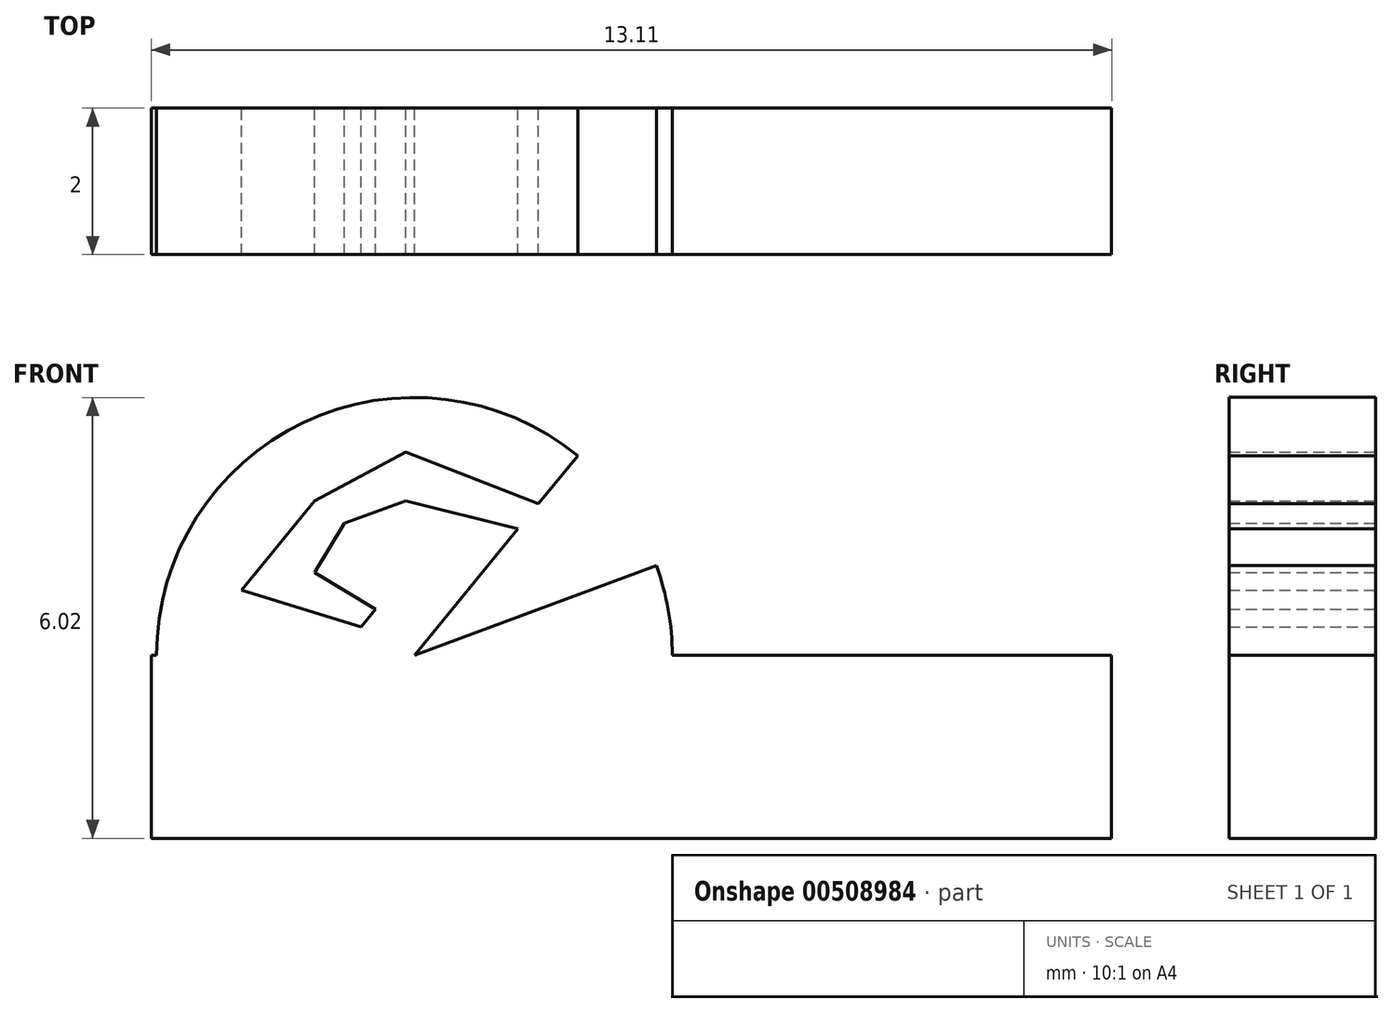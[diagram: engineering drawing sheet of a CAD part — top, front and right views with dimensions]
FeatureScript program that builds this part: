
annotation { "Feature Type Name" : "Feature", "Feature Type Description" : "" }
export const myFeature = defineFeature(function(context is Context, id is Id, definition is map)
    precondition{}
    {
        {
            var Q0;
            Q0=qCreatedBy(makeId("Front.planeOp"),FACE);
            var sketch = newSketch(context, id + "F0", { "sketchPlane" : qUnion([Q0])});
            skLineSegment(sketch, "E0.bottom", {"start": v(-10, 2.5) * mm, "end": v(10, 2.5) * mm});
            skLineSegment(sketch, "E0.top", {"start": v(-10, -2.5) * mm, "end": v(10, -2.5) * mm});
            skLineSegment(sketch, "E0.left", {"start": v(-10, 2.5) * mm, "end": v(-10, -2.5) * mm});
            skLineSegment(sketch, "E0.right", {"start": v(10, 2.5) * mm, "end": v(10, -2.5) * mm});
            skPoint(sketch, "E0.middle", {"position": v(0, 0) * mm});
            skArc(sketch, "E1", {"start": v(-2.89, 2.5) * mm, "mid": v(-2.94, 3.12) * mm, "end": v(-3.1, 3.72) * mm});
            skLineSegment(sketch, "E2", {"start": v(-4.18, 5.22) * mm, "end": v(-4.72, 4.57) * mm});
            skLineSegment(sketch, "E3", {"start": v(-6.41, 2.5) * mm, "end": v(-3.1, 3.72) * mm});
            skArc(sketch, "E4.trimOffspring", {"start": v(-4.18, 5.22) * mm, "mid": v(-7.92, 5.68) * mm, "end": v(-9.93, 2.5) * mm});
            skPoint(sketch, "E5.orphan", {"position": v(0, 4.87) * mm});
            skLineSegment(sketch, "E6", {"start": v(-4.72, 4.57) * mm, "end": v(-6.53, 5.28) * mm});
            skLineSegment(sketch, "E7", {"start": v(-6.53, 5.28) * mm, "end": v(-7.77, 4.6) * mm});
            skLineSegment(sketch, "E8", {"start": v(-7.77, 4.6) * mm, "end": v(-8.77, 3.39) * mm});
            skLineSegment(sketch, "E9", {"start": v(-8.77, 3.39) * mm, "end": v(-7.14, 2.89) * mm});
            skLineSegment(sketch, "E10", {"start": v(-7.14, 2.89) * mm, "end": v(-6.94, 3.13) * mm});
            skLineSegment(sketch, "E11", {"start": v(-6.94, 3.13) * mm, "end": v(-7.77, 3.63) * mm});
            skLineSegment(sketch, "E12", {"start": v(-7.77, 3.63) * mm, "end": v(-7.36, 4.3) * mm});
            skLineSegment(sketch, "E13", {"start": v(-7.36, 4.3) * mm, "end": v(-6.53, 4.6) * mm});
            skLineSegment(sketch, "E14", {"start": v(-6.53, 4.6) * mm, "end": v(-5, 4.23) * mm});
            skLineSegment(sketch, "E15.trimOffspring", {"start": v(-5, 4.23) * mm, "end": v(-6.41, 2.5) * mm});
            skSolve(sketch);
        }
        {
            var Q0;
            Q0=makeQuery(id+"F0.imprint","IMPRINT",FACE,{"disambiguationData":[TD([[makeQuery(id+"F0.imprint","IMPRINT",EDGE,{"derivedFrom":sQuery(id+"F0.wireOp",EDGE,"E0.top")}),1.0]])]});
            var Q1;
            Q1=makeQuery(id+"F0.imprint","IMPRINT",FACE,{"disambiguationData":[TD([[makeQuery(id+"F0.imprint","IMPRINT",EDGE,{"derivedFrom":sQuery(id+"F0.wireOp",EDGE,"E2")}),-1.0]])]});
            var Q2;
            {var subQ0=sQuery(id+"F0.wireOp",EDGE,"E1");Q2=makeQuery(id+"F0.imprint","IMPRINT",FACE,{"disambiguationData":[TD([[makeQuery(id+"F0.imprint","IMPRINT",EDGE,{"derivedFrom":subQ0}),1.0]])]});}
            extrude(context, id + "F1", {"entities" : qUnion([Q0, Q1, Q2]), "depth" : 2 * mm});
        }
        {
            var Q0;
            Q0=makeQuery(id+"F1.opExtrude","CAP_FACE",FACE,{"disambiguationData":[OSD([sQuery(id+"F0.wireOp",EDGE,"E0.bottom"),sQuery(id+"F0.wireOp",EDGE,"E0.top"),sQuery(id+"F0.wireOp",EDGE,"E0.left"),sQuery(id+"F0.wireOp",EDGE,"E0.right"),sQuery(id+"F0.wireOp",EDGE,"E1"),sQuery(id+"F0.wireOp",EDGE,"E2"),sQuery(id+"F0.wireOp",EDGE,"E3"),sQuery(id+"F0.wireOp",EDGE,"E4.trimOffspring"),sQuery(id+"F0.wireOp",EDGE,"E6"),sQuery(id+"F0.wireOp",EDGE,"E7"),sQuery(id+"F0.wireOp",EDGE,"E8"),sQuery(id+"F0.wireOp",EDGE,"E9"),sQuery(id+"F0.wireOp",EDGE,"E10"),sQuery(id+"F0.wireOp",EDGE,"E11"),sQuery(id+"F0.wireOp",EDGE,"E12"),sQuery(id+"F0.wireOp",EDGE,"E13"),sQuery(id+"F0.wireOp",EDGE,"E14"),sQuery(id+"F0.wireOp",EDGE,"E15.trimOffspring")])],"isStart":false});
            var sketch = newSketch(context, id + "F2", { "sketchPlane" : qUnion([Q0])});
            skLineSegment(sketch, "E16.bottom", {"start": v(-13.54, 0) * mm, "end": v(11.65, 0) * mm});
            skLineSegment(sketch, "E16.top", {"start": v(-13.54, -4.54) * mm, "end": v(11.65, -4.54) * mm});
            skLineSegment(sketch, "E16.left", {"start": v(-13.54, 0) * mm, "end": v(-13.54, -4.54) * mm});
            skLineSegment(sketch, "E16.right", {"start": v(11.65, 0) * mm, "end": v(11.65, -4.54) * mm});
            skLineSegment(sketch, "E17.bottom", {"start": v(3.1, 4.7) * mm, "end": v(11.65, 4.7) * mm});
            skLineSegment(sketch, "E17.top", {"start": v(3.1, -3.24) * mm, "end": v(11.65, -3.24) * mm});
            skLineSegment(sketch, "E17.left", {"start": v(3.1, 4.7) * mm, "end": v(3.1, -3.24) * mm});
            skLineSegment(sketch, "E17.right", {"start": v(11.65, 4.7) * mm, "end": v(11.65, -3.24) * mm});
            skLineSegment(sketch, "E18.bottom", {"start": v(-12.42, -0.74) * mm, "end": v(10.96, -0.74) * mm});
            skLineSegment(sketch, "E18.top", {"start": v(-12.42, -4.54) * mm, "end": v(10.96, -4.54) * mm});
            skLineSegment(sketch, "E18.left", {"start": v(-12.42, -0.74) * mm, "end": v(-12.42, -4.54) * mm});
            skLineSegment(sketch, "E18.right", {"start": v(10.96, -0.74) * mm, "end": v(10.96, -4.54) * mm});
            skSolve(sketch);
        }
        {
            var Q0;
            Q0 = qSketchRegion(id + "F2", true);
            var Q1;
            {var subQ0=sQuery(id+"F2.wireOp",EDGE,"E18.bottom");var subQ1=sQuery(id+"F2.wireOp",EDGE,"E17.left");var subQ2=makeQuery(id+"F2.imprint","INTERSECT",VERTEX,{"derivedFrom":[subQ1,subQ0]});Q1=makeQuery(id+"F2.imprint","IMPRINT",FACE,{"disambiguationData":[TD([[makeQuery(id+"F2.imprint","IMPRINT",EDGE,{"disambiguationData":[TD([[subQ2,-1.0]])],"derivedFrom":subQ1}),1.0]])]});}
            extrude(context, id + "F3", {"entities" : qUnion([Q0, Q1]), "operationType" : NewBodyOperationType.REMOVE, "oppositeDirection" : true, "depth" : 25 * mm});
        }
    });
